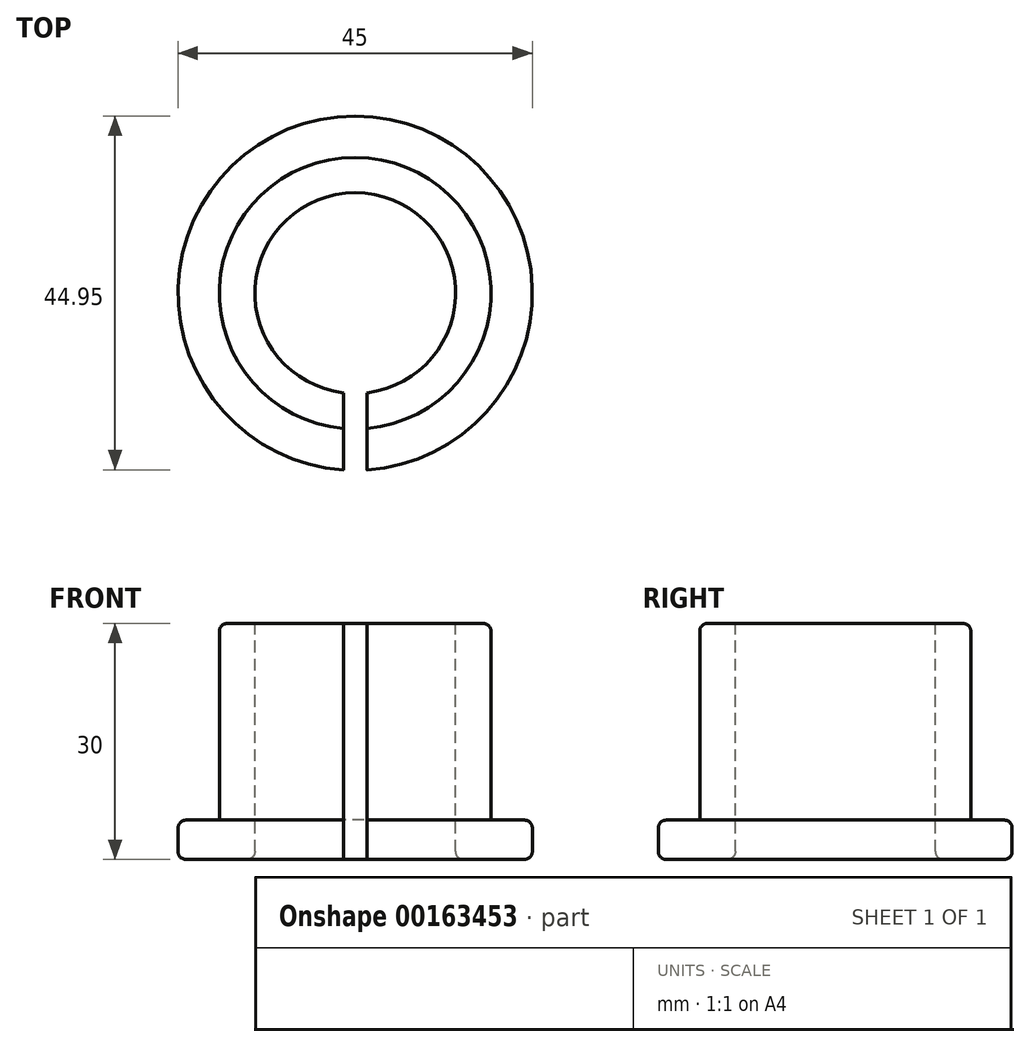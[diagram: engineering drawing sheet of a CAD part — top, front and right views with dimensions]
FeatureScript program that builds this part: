
annotation { "Feature Type Name" : "Feature", "Feature Type Description" : "" }
export const myFeature = defineFeature(function(context is Context, id is Id, definition is map)
    precondition{}
    {
        {
            var Q0;
            Q0=qCreatedBy(makeId("Top.planeOp"),FACE);
            var sketch = newSketch(context, id + "F0", { "sketchPlane" : qUnion([Q0]), "disableImprinting" : false});
            skCircle(sketch, "E0", {"center": v(0, 0) * mm, "radius": 22.5 * mm});
            skSolve(sketch);
        }
        {
            var Q0;
            Q0 = qSketchRegion(id + "F0", true);
            extrude(context, id + "F1", {"entities" : qUnion([Q0]), "depth" : 5 * mm});
        }
        {
            var Q0;
            Q0=makeQuery(id+"F1.opExtrude","CAP_FACE",FACE,{"disambiguationData":[OSD([sQuery(id+"F0.wireOp",EDGE,"E0")])],"isStart":false});
            var sketch = newSketch(context, id + "F2", { "sketchPlane" : qUnion([Q0]), "disableImprinting" : false});
            skCircle(sketch, "E1", {"center": v(0, 0) * mm, "radius": 17.25 * mm});
            skSolve(sketch);
        }
        {
            var Q0;
            Q0 = qSketchRegion(id + "F2", true);
            extrude(context, id + "F3", {"entities" : qUnion([Q0]), "operationType" : NewBodyOperationType.ADD, "depth" : 25 * mm});
        }
        {
            var Q0;
            Q0=makeQuery(id+"F3.opExtrude","CAP_FACE",FACE,{"disambiguationData":[OSD([sQuery(id+"F2.wireOp",EDGE,"E1")])],"isStart":false});
            var sketch = newSketch(context, id + "F4", { "sketchPlane" : qUnion([Q0]), "disableImprinting" : false});
            skCircle(sketch, "E2", {"center": v(0, 0) * mm, "radius": 12.75 * mm});
            skSolve(sketch);
        }
        {
            var Q0;
            Q0 = qSketchRegion(id + "F4", true);
            extrude(context, id + "F5", {"entities" : qUnion([Q0]), "operationType" : NewBodyOperationType.REMOVE, "endBound" : BoundingType.THROUGH_ALL, "oppositeDirection" : true, "depth" : 25 * mm});
        }
        {
            var Q0;
            Q0=makeQuery(id+"F1.opExtrude","CAP_FACE",FACE,{"disambiguationData":[OSD([sQuery(id+"F0.wireOp",EDGE,"E0")])],"isStart":true});
            var sketch = newSketch(context, id + "F6", { "sketchPlane" : qUnion([Q0])});
            skLineSegment(sketch, "E3.bottom", {"start": v(-1.5, 28.65) * mm, "end": v(1.5, 28.65) * mm});
            skLineSegment(sketch, "E3.top", {"start": v(-1.5, 0) * mm, "end": v(1.5, 0) * mm});
            skLineSegment(sketch, "E3.left", {"start": v(-1.5, 28.65) * mm, "end": v(-1.5, 0) * mm});
            skLineSegment(sketch, "E3.right", {"start": v(1.5, 28.65) * mm, "end": v(1.5, 0) * mm});
            skSolve(sketch);
        }
        {
            var Q0;
            Q0 = qSketchRegion(id + "F6", true);
            extrude(context, id + "F7", {"entities" : qUnion([Q0]), "operationType" : NewBodyOperationType.REMOVE, "endBound" : BoundingType.THROUGH_ALL, "oppositeDirection" : true, "depth" : 25 * mm});
        }
        {
            var Q0;
            Q0=makeQuery(id+"F3.opExtrude","CAP_EDGE",EDGE,{"disambiguationData":[OSD([sQuery(id+"F2.wireOp",EDGE,"E1")])],"isStart":false});
            var Q1;
            Q1=makeQuery(id+"F5.boolean.opBoolean","COPY",EDGE,{"derivedFrom":makeQuery(id+"F5.opExtrude","CAP_EDGE",EDGE,{"disambiguationData":[OSD([sQuery(id+"F4.wireOp",EDGE,"E2")])],"isStart":true})});
            var Q2;
            Q2=makeQuery(id+"F1.opExtrude","CAP_EDGE",EDGE,{"disambiguationData":[OSD([sQuery(id+"F0.wireOp",EDGE,"E0")])],"isStart":false});
            var Q3;
            Q3=makeQuery(id+"F1.opExtrude","CAP_EDGE",EDGE,{"disambiguationData":[OSD([sQuery(id+"F0.wireOp",EDGE,"E0")])],"isStart":true});
            var Q4;
            Q4=makeQuery(id+"F5.boolean.opBoolean","INTERSECT",EDGE,{"derivedFrom":[makeQuery(id+"F1.opExtrude","CAP_FACE",FACE,{"disambiguationData":[OSD([sQuery(id+"F0.wireOp",EDGE,"E0")])],"isStart":true}),makeQuery(id+"F5.opExtrude","SWEPT_FACE",FACE,{"disambiguationData":[OSD([sQuery(id+"F4.wireOp",EDGE,"E2")])]})]});
            fillet(context, id + "F8", {"entities" : qUnion([Q0, Q1, Q2, Q3, Q4]), "radius" : 1 * mm, "width" : 5 * mm, "tangentPropagation" : true, "blendControlType" : BlendControlType.RADIUS, "defaultsChanged" : true, "allowEdgeOverflow" : false, "vertexSettings" : [], "filletType" : FilletType.EDGE});
        }
    });
